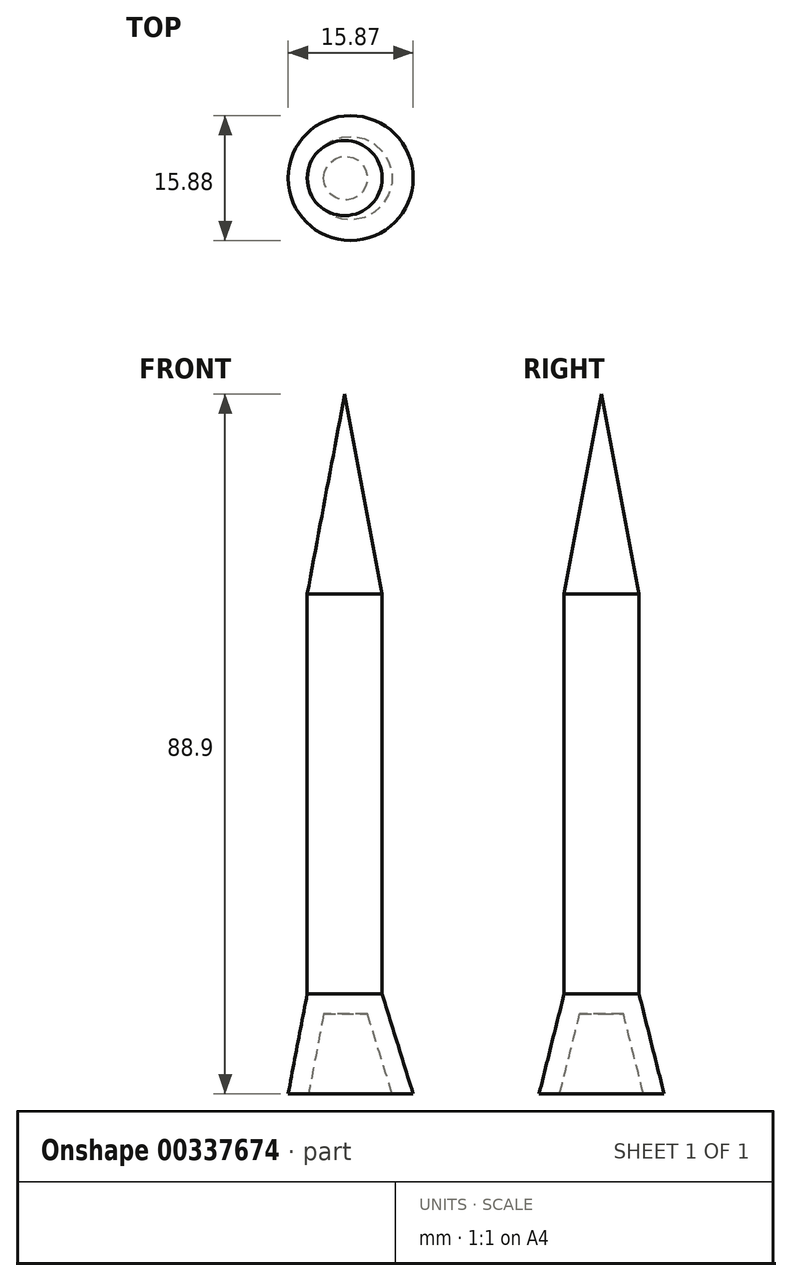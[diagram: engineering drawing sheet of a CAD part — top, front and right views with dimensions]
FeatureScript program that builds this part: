
annotation { "Feature Type Name" : "Feature", "Feature Type Description" : "" }
export const myFeature = defineFeature(function(context is Context, id is Id, definition is map)
    precondition{}
    {
        {
            var Q0;
            Q0=qCreatedBy(makeId("Top.planeOp"),FACE);
            var sketch = newSketch(context, id + "F0", { "sketchPlane" : qUnion([Q0])});
            skCircle(sketch, "E0", {"center": v(0, 0) * mm, "radius": 4.76 * mm});
            skSolve(sketch);
        }
        {
            var Q0;
            Q0=makeQuery(id+"F0.imprint","IMPRINT",FACE,{"disambiguationData":[TD([[makeQuery(id+"F0.imprint","IMPRINT",EDGE,{"derivedFrom":sQuery(id+"F0.wireOp",EDGE,"E0")}),1.0]])]});
            extrude(context, id + "F1", {"entities" : qUnion([Q0]), "depth" : 50.8 * mm});
        }
        {
            var Q0;
            Q0=makeQuery(id+"F1.opExtrude","CAP_FACE",FACE,{"disambiguationData":[OSD([sQuery(id+"F0.wireOp",EDGE,"E0")])],"isStart":false});
            var sketch = newSketch(context, id + "F2", { "sketchPlane" : qUnion([Q0])});
            skSolve(sketch);
        }
        {
            var Q0;
            Q0=makeQuery(id+"F2.imprint","IMPRINT",FACE,{"disambiguationData":[TD([[makeQuery(id+"F2.imprint","IMPRINT",EDGE,{"derivedFrom":makeQuery(id+"F1.opExtrude","CAP_EDGE",EDGE,{"disambiguationData":[OSD([sQuery(id+"F0.wireOp",EDGE,"E0")])],"isStart":false})}),1.0]])]});
            cPlane(context, id + "F3", {"entities" : qUnion([Q0]), "cplaneType" : CPlaneType.OFFSET, "offset" : 25.4 * mm, "width" : 152.4 * mm, "height" : 152.4 * mm});
        }
        {
            var Q0;
            Q0=qCreatedBy(id+"F3.planeOp",FACE);
            var sketch = newSketch(context, id + "F4", { "sketchPlane" : qUnion([Q0])});
            skPoint(sketch, "E1", {"position": v(0, 0) * mm});
            skSolve(sketch);
        }
        {
            var Q1;
            Q1=makeQuery(id+"F2.imprint","IMPRINT",FACE,{"disambiguationData":[TD([[makeQuery(id+"F2.imprint","IMPRINT",EDGE,{"derivedFrom":makeQuery(id+"F1.opExtrude","CAP_EDGE",EDGE,{"disambiguationData":[OSD([sQuery(id+"F0.wireOp",EDGE,"E0")])],"isStart":false})}),1.0]])]});
            var Q2;
            Q2=sQuery(id+"F4.wireOp",VERTEX,"E1");
            loft(context, id + "F5", {"operationType" : NewBodyOperationType.ADD, "sheetProfilesArray" : [{ "sheetProfileEntities" : qUnion([Q1]) }, { "sheetProfileEntities" : qUnion([Q2]) }]});
        }
        {
            var Q0;
            Q0=makeQuery(id+"F1.opExtrude","CAP_FACE",FACE,{"disambiguationData":[OSD([sQuery(id+"F0.wireOp",EDGE,"E0")])],"isStart":true});
            cPlane(context, id + "F6", {"entities" : qUnion([Q0]), "cplaneType" : CPlaneType.OFFSET, "offset" : 12.7 * mm, "width" : 152.4 * mm, "height" : 152.4 * mm});
        }
        {
            var Q0;
            Q0=qCreatedBy(id+"F6.planeOp",FACE);
            var sketch = newSketch(context, id + "F7", { "sketchPlane" : qUnion([Q0])});
            skCircle(sketch, "E2", {"center": v(0.75, 0) * mm, "radius": 7.94 * mm});
            skSolve(sketch);
        }
        {
            var Q0;
            Q0=makeQuery(id+"F1.opExtrude","CAP_FACE",FACE,{"disambiguationData":[OSD([sQuery(id+"F0.wireOp",EDGE,"E0")])],"isStart":true});
            var Q1;
            Q1=makeQuery(id+"F7.imprint","IMPRINT",FACE,{"disambiguationData":[TD([[makeQuery(id+"F7.imprint","IMPRINT",EDGE,{"derivedFrom":sQuery(id+"F7.wireOp",EDGE,"E2")}),1.0]])]});
            loft(context, id + "F8", {"sheetProfilesArray" : [{ "sheetProfileEntities" : qUnion([Q0]) }, { "sheetProfileEntities" : qUnion([Q1]) }]});
        }
        {
            var Q0;
            Q0=makeQuery(id+"F8.opLoft","CAP_FACE",FACE,{"disambiguationData":[OSD([makeQuery(id+"F7.imprint","IMPRINT",FACE,{"disambiguationData":[TD([[makeQuery(id+"F7.imprint","IMPRINT",EDGE,{"derivedFrom":sQuery(id+"F7.wireOp",EDGE,"E2")}),1.0]])]})])],"isStart":true});
            shell(context, id + "F9", {"entities" : qUnion([Q0]), "thickness" : 2.54 * mm});
        }
    });
